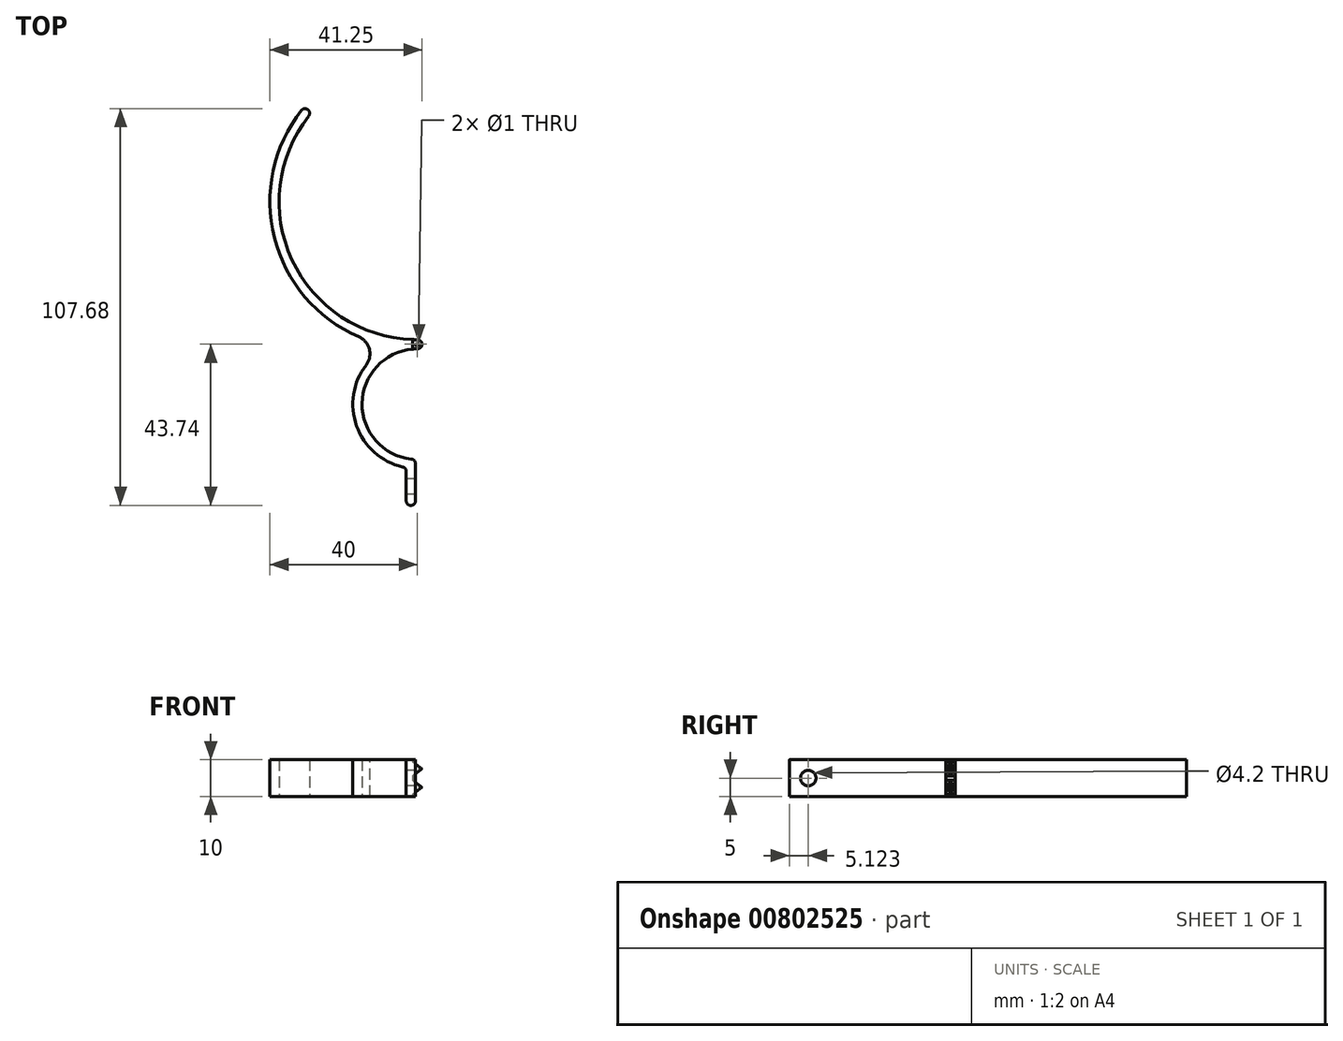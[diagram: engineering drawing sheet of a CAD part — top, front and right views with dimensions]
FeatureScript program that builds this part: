
annotation { "Feature Type Name" : "Feature", "Feature Type Description" : "" }
export const myFeature = defineFeature(function(context is Context, id is Id, definition is map)
    precondition{}
    {
        {
            var Q0;
            Q0=qCreatedBy(makeId("Top.planeOp"),FACE);
            var sketch = newSketch(context, id + "F0", { "sketchPlane" : qUnion([Q0])});
            skCircle(sketch, "E0", {"center": v(0, 0) * mm, "radius": 1.25 * mm});
            skArc(sketch, "E1", {"start": v(0, -1.25) * mm, "mid": v(-15, -16) * mm, "end": v(-0.5, -31.24) * mm});
            skArc(sketch, "E2.0", {"start": v(0, 1.25) * mm, "mid": v(-17.5, -16) * mm, "end": v(-0.5, -33.74) * mm});
            skArc(sketch, "E3", {"start": v(0, 76.25) * mm, "mid": v(-37.5, 38.75) * mm, "end": v(0, 1.25) * mm});
            skArc(sketch, "E4.0", {"start": v(0, 78.75) * mm, "mid": v(-40, 38.75) * mm, "end": v(0, -1.25) * mm});
            skLineSegment(sketch, "E5", {"start": v(0, 78.75) * mm, "end": v(0, 76.25) * mm});
            skLineSegment(sketch, "E6.bottom", {"start": v(-0.5, -31.24) * mm, "end": v(-3, -31.24) * mm});
            skLineSegment(sketch, "E6.top", {"start": v(-0.5, -43.74) * mm, "end": v(-3, -43.74) * mm});
            skLineSegment(sketch, "E6.left", {"start": v(-0.5, -31.24) * mm, "end": v(-0.5, -43.74) * mm});
            skLineSegment(sketch, "E6.right", {"start": v(-3, -31.24) * mm, "end": v(-3, -43.74) * mm});
            skPoint(sketch, "E7", {"position": v(-0.5, -33.74) * mm});
            skPoint(sketch, "E8.orphan", {"position": v(0, -31.25) * mm});
            skSolve(sketch);
        }
        {
            var Q0;
            Q0=qSketchRegion(id+"F0",true);
            extrude(context, id + "F1", {"entities" : qUnion([Q0]), "depth" : 10 * mm, "offsetDistance" : 25 * mm});
        }
        {
            var Q0;
            Q0=qCreatedBy(makeId("Top.planeOp"),FACE);
            var sketch = newSketch(context, id + "F2", { "sketchPlane" : qUnion([Q0])});
            skLineSegment(sketch, "E9.bottom", {"start": v(-26.52, 65.27) * mm, "end": v(26.52, 65.27) * mm, "construction": true});
            skLineSegment(sketch, "E9.top", {"start": v(-26.52, 12.23) * mm, "end": v(26.52, 12.23) * mm, "construction": true});
            skLineSegment(sketch, "E9.left", {"start": v(-26.52, 65.27) * mm, "end": v(-26.52, 12.23) * mm, "construction": true});
            skLineSegment(sketch, "E9.right", {"start": v(26.52, 65.27) * mm, "end": v(26.52, 12.23) * mm, "construction": true});
            skPoint(sketch, "E10", {"position": v(0, 65.27) * mm});
            skLineSegment(sketch, "E11.bottom", {"start": v(-26.52, 65.27) * mm, "end": v(26.52, 65.27) * mm});
            skLineSegment(sketch, "E11.top", {"start": v(-26.52, 78.75) * mm, "end": v(26.52, 78.75) * mm});
            skLineSegment(sketch, "E11.left", {"start": v(-26.52, 65.27) * mm, "end": v(-26.52, 78.75) * mm});
            skLineSegment(sketch, "E11.right", {"start": v(26.52, 65.27) * mm, "end": v(26.52, 78.75) * mm});
            skSolve(sketch);
        }
        {
            var Q0;
            Q0=makeQuery(id+"F2.imprint","IMPRINT",FACE,{"disambiguationData":[TD([[makeQuery(id+"F2.imprint","IMPRINT",EDGE,{"derivedFrom":sQuery(id+"F2.wireOp",EDGE,"E11.bottom")}),1.0]])]});
            var Q1;
            Q1=makeQuery(id+"F1.opExtrude","CAP_FACE",FACE,{"disambiguationData":[OSD([sQuery(id+"F0.wireOp",EDGE,"E0"),sQuery(id+"F0.wireOp",EDGE,"E1"),sQuery(id+"F0.wireOp",EDGE,"E2.0"),sQuery(id+"F0.wireOp",EDGE,"E3"),sQuery(id+"F0.wireOp",EDGE,"E4.0"),sQuery(id+"F0.wireOp",EDGE,"E5"),sQuery(id+"F0.wireOp",EDGE,"E6.top"),sQuery(id+"F0.wireOp",EDGE,"E6.left"),sQuery(id+"F0.wireOp",EDGE,"E6.right")])],"isStart":false});
            extrude(context, id + "F3", {"entities" : qUnion([Q0]), "operationType" : NewBodyOperationType.REMOVE, "endBound" : BoundingType.UP_TO_SURFACE, "depth" : 25 * mm, "endBoundEntityFace" : qUnion([Q1]), "offsetDistance" : 25 * mm});
        }
        {
            var Q0;
            Q0=makeQuery(id+"F1.opExtrude","CAP_FACE",FACE,{"disambiguationData":[OSD([sQuery(id+"F0.wireOp",EDGE,"E0"),sQuery(id+"F0.wireOp",EDGE,"E1"),sQuery(id+"F0.wireOp",EDGE,"E2.0"),sQuery(id+"F0.wireOp",EDGE,"E3"),sQuery(id+"F0.wireOp",EDGE,"E4.0"),sQuery(id+"F0.wireOp",EDGE,"E5"),sQuery(id+"F0.wireOp",EDGE,"E6.top"),sQuery(id+"F0.wireOp",EDGE,"E6.left"),sQuery(id+"F0.wireOp",EDGE,"E6.right")])],"isStart":false});
            var sketch = newSketch(context, id + "F4", { "sketchPlane" : qUnion([Q0])});
            skCircle(sketch, "E12", {"center": v(0, 0) * mm, "radius": 0.5 * mm});
            skSolve(sketch);
        }
        {
            var Q0;
            Q0=makeQuery(id+"F4.imprint","IMPRINT",FACE,{"disambiguationData":[TD([[makeQuery(id+"F4.imprint","IMPRINT",EDGE,{"derivedFrom":sQuery(id+"F4.wireOp",EDGE,"E12")}),1.0]])]});
            var Q1;
            Q1=sQuery(id+"F4.wireOp",EDGE,"E12");
            extrude(context, id + "F5", {"entities" : qUnion([Q0]), "operationType" : NewBodyOperationType.REMOVE, "surfaceEntities" : qUnion([Q1]), "endBound" : BoundingType.UP_TO_NEXT, "oppositeDirection" : true, "depth" : 25 * mm, "offsetDistance" : 25 * mm});
        }
        {
            var Q0;
            Q0=makeQuery(id+"F1.opExtrude","SWEPT_FACE",FACE,{"disambiguationData":[OSD([sQuery(id+"F0.wireOp",EDGE,"E6.right")])]});
            var sketch = newSketch(context, id + "F6", { "sketchPlane" : qUnion([Q0])});
            skCircle(sketch, "E13", {"center": v(38.62, 5) * mm, "radius": 2.1 * mm});
            skSolve(sketch);
        }
        {
            var Q0;
            Q0=makeQuery(id+"F6.imprint","IMPRINT",FACE,{"disambiguationData":[TD([[makeQuery(id+"F6.imprint","IMPRINT",EDGE,{"derivedFrom":sQuery(id+"F6.wireOp",EDGE,"E13")}),1.0]])]});
            extrude(context, id + "F7", {"entities" : qUnion([Q0]), "operationType" : NewBodyOperationType.REMOVE, "endBound" : BoundingType.UP_TO_NEXT, "oppositeDirection" : true, "depth" : 25 * mm, "offsetDistance" : 25 * mm});
        }
        {
            var Q0;
            Q0=makeQuery(id+"F3.boolean.opBoolean","INTERSECT",EDGE,{"derivedFrom":[makeQuery(id+"F1.opExtrude","SWEPT_FACE",FACE,{"disambiguationData":[OSD([sQuery(id+"F0.wireOp",EDGE,"E4.0")])]}),makeQuery(id+"F3.opExtrude","SWEPT_FACE",FACE,{"disambiguationData":[OSD([sQuery(id+"F2.wireOp",EDGE,"E11.left")])]})]});
            var Q1;
            Q1=makeQuery(id+"F1.opExtrude","SWEPT_EDGE",EDGE,{"disambiguationData":[OSD([sQuery(id+"F0.wireOp",EDGE,"E2.0"),sQuery(id+"F0.wireOp",EDGE,"E4.0")])]});
            fillet(context, id + "F8", {"entities" : qUnion([Q0, Q1]), "radius" : 5 * mm, "tangentPropagation" : true, "allowEdgeOverflow" : false});
        }
        {
            var Q0;
            Q0=makeQuery(id+"F1.opExtrude","SWEPT_EDGE",EDGE,{"disambiguationData":[OSD([sQuery(id+"F0.wireOp",EDGE,"E2.0"),sQuery(id+"F0.wireOp",EDGE,"E6.right")])]});
            var Q1;
            Q1=makeQuery(id+"F1.opExtrude","SWEPT_EDGE",EDGE,{"disambiguationData":[OSD([sQuery(id+"F0.wireOp",EDGE,"E1"),sQuery(id+"F0.wireOp",EDGE,"E6.bottom"),sQuery(id+"F0.wireOp",EDGE,"E6.left")])]});
            var Q2;
            Q2=makeQuery(id+"F1.opExtrude","SWEPT_EDGE",EDGE,{"disambiguationData":[OSD([sQuery(id+"F0.wireOp",EDGE,"E6.top"),sQuery(id+"F0.wireOp",EDGE,"E6.left")])]});
            var Q3;
            Q3=makeQuery(id+"F1.opExtrude","SWEPT_EDGE",EDGE,{"disambiguationData":[OSD([sQuery(id+"F0.wireOp",EDGE,"E6.top"),sQuery(id+"F0.wireOp",EDGE,"E6.right")])]});
            var Q4;
            Q4=makeQuery(id+"F8.opFillet","BLEND_EDGE",EDGE,{"blendedFrom":[makeQuery(id+"F3.boolean.opBoolean","INTERSECT",EDGE,{"derivedFrom":[makeQuery(id+"F1.opExtrude","SWEPT_FACE",FACE,{"disambiguationData":[OSD([sQuery(id+"F0.wireOp",EDGE,"E4.0")])]}),makeQuery(id+"F3.opExtrude","SWEPT_FACE",FACE,{"disambiguationData":[OSD([sQuery(id+"F2.wireOp",EDGE,"E11.left")])]})]}),makeQuery(id+"F1.opExtrude","SWEPT_FACE",FACE,{"disambiguationData":[OSD([sQuery(id+"F0.wireOp",EDGE,"E3")])]})],"blendedInto":[makeQuery(id+"F1.opExtrude","SWEPT_FACE",FACE,{"disambiguationData":[OSD([sQuery(id+"F0.wireOp",EDGE,"E3")])]})]});
            fillet(context, id + "F9", {"entities" : qUnion([Q0, Q1, Q2, Q3, Q4]), "radius" : 1.25 * mm, "tangentPropagation" : true, "allowEdgeOverflow" : false});
        }
        {
            var Q0;
            Q0=qCreatedBy(makeId("Front.planeOp"),FACE);
            var sketch = newSketch(context, id + "F10", { "sketchPlane" : qUnion([Q0])});
            skLineSegment(sketch, "E14", {"start": v(1.25, 2.5) * mm, "end": v(-1.25, 0.58) * mm});
            skLineSegment(sketch, "E15", {"start": v(-1.25, 4.42) * mm, "end": v(1.25, 2.5) * mm});
            skLineSegment(sketch, "E16.0.0", {"start": v(0, 0) * mm, "end": v(1.25, 0) * mm, "construction": true});
            skLineSegment(sketch, "E16.0.1", {"start": v(0, 0) * mm, "end": v(0, 10) * mm, "construction": true});
            skLineSegment(sketch, "E16.0.2", {"start": v(0, 10) * mm, "end": v(1.25, 10) * mm, "construction": true});
            skLineSegment(sketch, "E16.0.3", {"start": v(0, 10) * mm, "end": v(0, 0) * mm, "construction": true});
            skPoint(sketch, "E17", {"position": v(0, 2.5) * mm});
            skLineSegment(sketch, "E18", {"start": v(-1.25, 4.42) * mm, "end": v(-1.25, 0.58) * mm, "construction": true});
            skLineSegment(sketch, "E19", {"start": v(0, 5) * mm, "end": v(1.25, 5) * mm, "construction": true});
            skLineSegment(sketch, "E20", {"start": v(1.25, 2.5) * mm, "end": v(-1.25, 2.5) * mm, "construction": true});
            skLineSegment(sketch, "E21.MirrorCS", {"start": v(-1.25, 5.58) * mm, "end": v(1.25, 7.5) * mm});
            skLineSegment(sketch, "E22.MirrorCS", {"start": v(1.25, 7.5) * mm, "end": v(-1.25, 9.42) * mm});
            skLineSegment(sketch, "E23", {"start": v(-1.25, 9.42) * mm, "end": v(-1.25, 10) * mm});
            skLineSegment(sketch, "E24", {"start": v(-1.25, 10) * mm, "end": v(1.25, 10) * mm});
            skLineSegment(sketch, "E25", {"start": v(1.25, 7.5) * mm, "end": v(1.25, 10) * mm});
            skLineSegment(sketch, "E26", {"start": v(-1.25, 5.58) * mm, "end": v(-1.25, 4.42) * mm});
            skLineSegment(sketch, "E27", {"start": v(-1.25, 0.58) * mm, "end": v(-1.25, 0) * mm});
            skLineSegment(sketch, "E28", {"start": v(-1.25, 0) * mm, "end": v(1.25, 0) * mm});
            skLineSegment(sketch, "E29", {"start": v(1.25, 2.5) * mm, "end": v(1.25, 0) * mm});
            skLineSegment(sketch, "E30", {"start": v(1.25, 7.5) * mm, "end": v(1.25, 2.5) * mm});
            skSolve(sketch);
        }
        {
            var Q0;
            Q0 = qSketchRegion(id + "F10", true);
            extrude(context, id + "F11", {"entities" : qUnion([Q0]), "operationType" : NewBodyOperationType.REMOVE, "oppositeDirection" : true, "depth" : 5 * mm, "offsetDistance" : 25 * mm, "hasSecondDirection" : true, "secondDirectionOppositeDirection" : false, "secondDirectionDepth" : 5 * mm});
        }
    });
